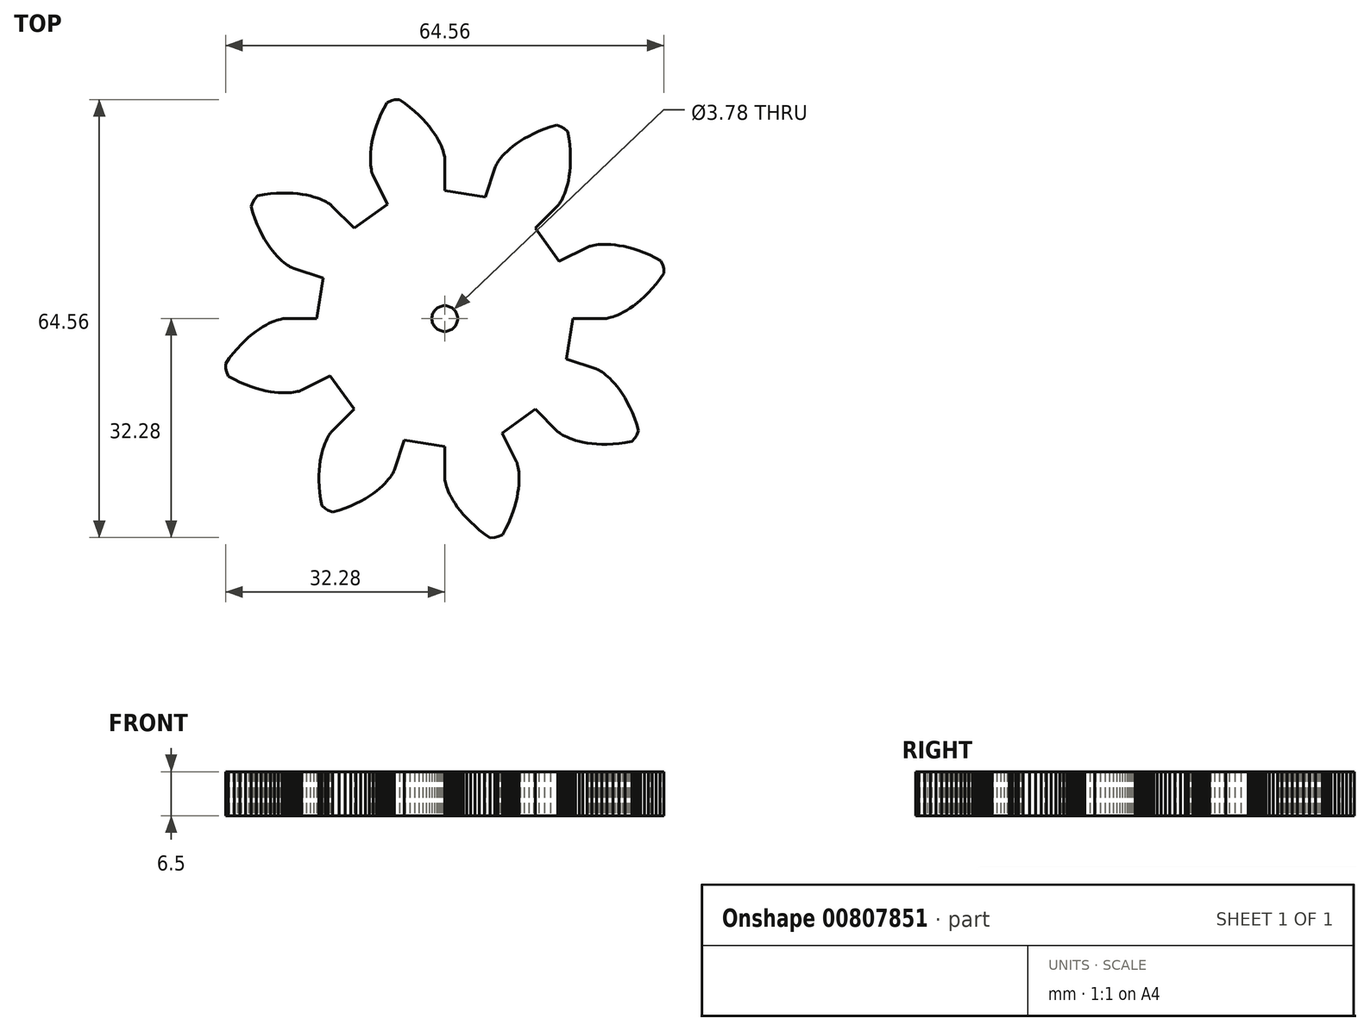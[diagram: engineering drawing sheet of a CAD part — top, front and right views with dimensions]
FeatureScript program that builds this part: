
annotation { "Feature Type Name" : "Feature", "Feature Type Description" : "" }
export const myFeature = defineFeature(function(context is Context, id is Id, definition is map)
    precondition{}
    {
        {
            var Q0;
            Q0=qCreatedBy(makeId("Top.planeOp"),FACE);
            var sketch = newSketch(context, id + "F0", { "sketchPlane" : qUnion([Q0])});
            skLineSegment(sketch, "E0", {"start": v(18.85, 0) * mm, "end": v(23.58, 0) * mm});
            skLineSegment(sketch, "E1", {"start": v(23.58, 0) * mm, "end": v(23.62, 0) * mm});
            skLineSegment(sketch, "E2", {"start": v(23.62, 0) * mm, "end": v(23.7, 0) * mm});
            skLineSegment(sketch, "E3", {"start": v(23.7, 0) * mm, "end": v(23.83, 0.03) * mm});
            skLineSegment(sketch, "E4", {"start": v(23.83, 0.03) * mm, "end": v(24, 0.05) * mm});
            skLineSegment(sketch, "E5", {"start": v(24, 0.05) * mm, "end": v(24.22, 0.1) * mm});
            skLineSegment(sketch, "E6", {"start": v(24.22, 0.1) * mm, "end": v(24.48, 0.17) * mm});
            skLineSegment(sketch, "E7", {"start": v(24.48, 0.17) * mm, "end": v(24.77, 0.26) * mm});
            skLineSegment(sketch, "E8", {"start": v(24.77, 0.26) * mm, "end": v(25.1, 0.38) * mm});
            skLineSegment(sketch, "E9", {"start": v(25.1, 0.38) * mm, "end": v(25.47, 0.53) * mm});
            skLineSegment(sketch, "E10", {"start": v(25.47, 0.53) * mm, "end": v(25.88, 0.72) * mm});
            skLineSegment(sketch, "E11", {"start": v(25.88, 0.72) * mm, "end": v(26.31, 0.94) * mm});
            skLineSegment(sketch, "E12", {"start": v(26.31, 0.94) * mm, "end": v(26.78, 1.2) * mm});
            skLineSegment(sketch, "E13", {"start": v(26.78, 1.2) * mm, "end": v(27.27, 1.52) * mm});
            skLineSegment(sketch, "E14", {"start": v(27.27, 1.52) * mm, "end": v(27.78, 1.87) * mm});
            skLineSegment(sketch, "E15", {"start": v(27.78, 1.87) * mm, "end": v(28.31, 2.28) * mm});
            skLineSegment(sketch, "E16", {"start": v(28.31, 2.28) * mm, "end": v(28.86, 2.73) * mm});
            skLineSegment(sketch, "E17", {"start": v(28.86, 2.73) * mm, "end": v(29.42, 3.25) * mm});
            skLineSegment(sketch, "E18", {"start": v(29.42, 3.25) * mm, "end": v(30, 3.81) * mm});
            skLineSegment(sketch, "E19", {"start": v(30, 3.81) * mm, "end": v(30.57, 4.43) * mm});
            skLineSegment(sketch, "E20", {"start": v(30.57, 4.43) * mm, "end": v(31.14, 5.12) * mm});
            skLineSegment(sketch, "E21", {"start": v(31.14, 5.12) * mm, "end": v(31.72, 5.86) * mm});
            skLineSegment(sketch, "E22", {"start": v(31.72, 5.86) * mm, "end": v(32.28, 6.66) * mm});
            skLineSegment(sketch, "E23", {"start": v(32.28, 6.66) * mm, "end": v(32.24, 7.39) * mm});
            skLineSegment(sketch, "E24", {"start": v(32.24, 7.39) * mm, "end": v(32.13, 7.83) * mm});
            skLineSegment(sketch, "E25", {"start": v(32.13, 7.83) * mm, "end": v(31.85, 8.5) * mm});
            skLineSegment(sketch, "E26", {"start": v(31.85, 8.5) * mm, "end": v(30.98, 8.97) * mm});
            skLineSegment(sketch, "E27", {"start": v(30.98, 8.97) * mm, "end": v(30.14, 9.37) * mm});
            skLineSegment(sketch, "E28", {"start": v(30.14, 9.37) * mm, "end": v(29.31, 9.73) * mm});
            skLineSegment(sketch, "E29", {"start": v(29.31, 9.73) * mm, "end": v(28.52, 10.03) * mm});
            skLineSegment(sketch, "E30", {"start": v(28.52, 10.03) * mm, "end": v(27.76, 10.28) * mm});
            skLineSegment(sketch, "E31", {"start": v(27.76, 10.28) * mm, "end": v(27.03, 10.48) * mm});
            skLineSegment(sketch, "E32", {"start": v(27.03, 10.48) * mm, "end": v(26.33, 10.64) * mm});
            skLineSegment(sketch, "E33", {"start": v(26.33, 10.64) * mm, "end": v(25.68, 10.77) * mm});
            skLineSegment(sketch, "E34", {"start": v(25.68, 10.77) * mm, "end": v(25.06, 10.85) * mm});
            skLineSegment(sketch, "E35", {"start": v(25.06, 10.85) * mm, "end": v(24.48, 10.91) * mm});
            skLineSegment(sketch, "E36", {"start": v(24.48, 10.91) * mm, "end": v(23.95, 10.94) * mm});
            skLineSegment(sketch, "E37", {"start": v(23.95, 10.94) * mm, "end": v(23.46, 10.95) * mm});
            skLineSegment(sketch, "E38", {"start": v(23.46, 10.95) * mm, "end": v(23.02, 10.93) * mm});
            skLineSegment(sketch, "E39", {"start": v(23.02, 10.93) * mm, "end": v(22.62, 10.9) * mm});
            skLineSegment(sketch, "E40", {"start": v(22.62, 10.9) * mm, "end": v(22.26, 10.86) * mm});
            skLineSegment(sketch, "E41", {"start": v(22.26, 10.86) * mm, "end": v(21.96, 10.81) * mm});
            skLineSegment(sketch, "E42", {"start": v(21.96, 10.81) * mm, "end": v(21.7, 10.76) * mm});
            skLineSegment(sketch, "E43", {"start": v(21.7, 10.76) * mm, "end": v(21.49, 10.7) * mm});
            skLineSegment(sketch, "E44", {"start": v(21.49, 10.7) * mm, "end": v(21.32, 10.65) * mm});
            skLineSegment(sketch, "E45", {"start": v(21.32, 10.65) * mm, "end": v(21.2, 10.6) * mm});
            skLineSegment(sketch, "E46", {"start": v(21.2, 10.6) * mm, "end": v(21.12, 10.58) * mm});
            skLineSegment(sketch, "E47", {"start": v(21.12, 10.58) * mm, "end": v(21.08, 10.56) * mm});
            skLineSegment(sketch, "E48", {"start": v(21.08, 10.56) * mm, "end": v(16.85, 8.44) * mm});
            skLineSegment(sketch, "E49", {"start": v(16.85, 8.44) * mm, "end": v(13.33, 13.33) * mm});
            skLineSegment(sketch, "E50", {"start": v(13.33, 13.33) * mm, "end": v(16.67, 16.67) * mm});
            skLineSegment(sketch, "E51", {"start": v(16.67, 16.67) * mm, "end": v(16.7, 16.7) * mm});
            skLineSegment(sketch, "E52", {"start": v(16.7, 16.7) * mm, "end": v(16.75, 16.77) * mm});
            skLineSegment(sketch, "E53", {"start": v(16.75, 16.77) * mm, "end": v(16.83, 16.87) * mm});
            skLineSegment(sketch, "E54", {"start": v(16.83, 16.87) * mm, "end": v(16.93, 17.01) * mm});
            skLineSegment(sketch, "E55", {"start": v(16.93, 17.01) * mm, "end": v(17.05, 17.2) * mm});
            skLineSegment(sketch, "E56", {"start": v(17.05, 17.2) * mm, "end": v(17.19, 17.43) * mm});
            skLineSegment(sketch, "E57", {"start": v(17.19, 17.43) * mm, "end": v(17.33, 17.7) * mm});
            skLineSegment(sketch, "E58", {"start": v(17.33, 17.7) * mm, "end": v(17.48, 18.02) * mm});
            skLineSegment(sketch, "E59", {"start": v(17.48, 18.02) * mm, "end": v(17.64, 18.39) * mm});
            skLineSegment(sketch, "E60", {"start": v(17.64, 18.39) * mm, "end": v(17.8, 18.8) * mm});
            skLineSegment(sketch, "E61", {"start": v(17.8, 18.8) * mm, "end": v(17.94, 19.27) * mm});
            skLineSegment(sketch, "E62", {"start": v(17.94, 19.27) * mm, "end": v(18.08, 19.79) * mm});
            skLineSegment(sketch, "E63", {"start": v(18.08, 19.79) * mm, "end": v(18.2, 20.35) * mm});
            skLineSegment(sketch, "E64", {"start": v(18.2, 20.35) * mm, "end": v(18.32, 20.97) * mm});
            skLineSegment(sketch, "E65", {"start": v(18.32, 20.97) * mm, "end": v(18.4, 21.63) * mm});
            skLineSegment(sketch, "E66", {"start": v(18.4, 21.63) * mm, "end": v(18.47, 22.34) * mm});
            skLineSegment(sketch, "E67", {"start": v(18.47, 22.34) * mm, "end": v(18.5, 23.1) * mm});
            skLineSegment(sketch, "E68", {"start": v(18.5, 23.1) * mm, "end": v(18.51, 23.9) * mm});
            skLineSegment(sketch, "E69", {"start": v(18.51, 23.9) * mm, "end": v(18.48, 24.75) * mm});
            skLineSegment(sketch, "E70", {"start": v(18.48, 24.75) * mm, "end": v(18.4, 25.64) * mm});
            skLineSegment(sketch, "E71", {"start": v(18.4, 25.64) * mm, "end": v(18.29, 26.57) * mm});
            skLineSegment(sketch, "E72", {"start": v(18.29, 26.57) * mm, "end": v(18.12, 27.54) * mm});
            skLineSegment(sketch, "E73", {"start": v(18.12, 27.54) * mm, "end": v(17.57, 28.02) * mm});
            skLineSegment(sketch, "E74", {"start": v(17.57, 28.02) * mm, "end": v(17.18, 28.26) * mm});
            skLineSegment(sketch, "E75", {"start": v(17.18, 28.26) * mm, "end": v(16.5, 28.53) * mm});
            skLineSegment(sketch, "E76", {"start": v(16.5, 28.53) * mm, "end": v(15.57, 28.25) * mm});
            skLineSegment(sketch, "E77", {"start": v(15.57, 28.25) * mm, "end": v(14.68, 27.94) * mm});
            skLineSegment(sketch, "E78", {"start": v(14.68, 27.94) * mm, "end": v(13.85, 27.6) * mm});
            skLineSegment(sketch, "E79", {"start": v(13.85, 27.6) * mm, "end": v(13.08, 27.26) * mm});
            skLineSegment(sketch, "E80", {"start": v(13.08, 27.26) * mm, "end": v(12.36, 26.9) * mm});
            skLineSegment(sketch, "E81", {"start": v(12.36, 26.9) * mm, "end": v(11.7, 26.52) * mm});
            skLineSegment(sketch, "E82", {"start": v(11.7, 26.52) * mm, "end": v(11.1, 26.15) * mm});
            skLineSegment(sketch, "E83", {"start": v(11.1, 26.15) * mm, "end": v(10.54, 25.77) * mm});
            skLineSegment(sketch, "E84", {"start": v(10.54, 25.77) * mm, "end": v(10.04, 25.4) * mm});
            skLineSegment(sketch, "E85", {"start": v(10.04, 25.4) * mm, "end": v(9.6, 25.03) * mm});
            skLineSegment(sketch, "E86", {"start": v(9.6, 25.03) * mm, "end": v(9.2, 24.67) * mm});
            skLineSegment(sketch, "E87", {"start": v(9.2, 24.67) * mm, "end": v(8.85, 24.33) * mm});
            skLineSegment(sketch, "E88", {"start": v(8.85, 24.33) * mm, "end": v(8.54, 24) * mm});
            skLineSegment(sketch, "E89", {"start": v(8.54, 24) * mm, "end": v(8.28, 23.7) * mm});
            skLineSegment(sketch, "E90", {"start": v(8.28, 23.7) * mm, "end": v(8.06, 23.42) * mm});
            skLineSegment(sketch, "E91", {"start": v(8.06, 23.42) * mm, "end": v(7.88, 23.17) * mm});
            skLineSegment(sketch, "E92", {"start": v(7.88, 23.17) * mm, "end": v(7.74, 22.95) * mm});
            skLineSegment(sketch, "E93", {"start": v(7.74, 22.95) * mm, "end": v(7.63, 22.76) * mm});
            skLineSegment(sketch, "E94", {"start": v(7.63, 22.76) * mm, "end": v(7.54, 22.6) * mm});
            skLineSegment(sketch, "E95", {"start": v(7.54, 22.6) * mm, "end": v(7.49, 22.49) * mm});
            skLineSegment(sketch, "E96", {"start": v(7.49, 22.49) * mm, "end": v(7.45, 22.41) * mm});
            skLineSegment(sketch, "E97", {"start": v(7.45, 22.41) * mm, "end": v(7.44, 22.37) * mm});
            skLineSegment(sketch, "E98", {"start": v(7.44, 22.37) * mm, "end": v(5.95, 17.89) * mm});
            skLineSegment(sketch, "E99", {"start": v(5.95, 17.89) * mm, "end": v(0, 18.85) * mm});
            skLineSegment(sketch, "E100", {"start": v(0, 18.85) * mm, "end": v(0, 23.58) * mm});
            skLineSegment(sketch, "E101", {"start": v(0, 23.58) * mm, "end": v(0, 23.62) * mm});
            skLineSegment(sketch, "E102", {"start": v(0, 23.62) * mm, "end": v(0, 23.7) * mm});
            skLineSegment(sketch, "E103", {"start": v(0, 23.7) * mm, "end": v(-0.03, 23.83) * mm});
            skLineSegment(sketch, "E104", {"start": v(-0.03, 23.83) * mm, "end": v(-0.06, 24) * mm});
            skLineSegment(sketch, "E105", {"start": v(-0.06, 24) * mm, "end": v(-0.1, 24.22) * mm});
            skLineSegment(sketch, "E106", {"start": v(-0.1, 24.22) * mm, "end": v(-0.17, 24.48) * mm});
            skLineSegment(sketch, "E107", {"start": v(-0.17, 24.48) * mm, "end": v(-0.26, 24.77) * mm});
            skLineSegment(sketch, "E108", {"start": v(-0.26, 24.77) * mm, "end": v(-0.38, 25.1) * mm});
            skLineSegment(sketch, "E109", {"start": v(-0.38, 25.1) * mm, "end": v(-0.53, 25.47) * mm});
            skLineSegment(sketch, "E110", {"start": v(-0.53, 25.47) * mm, "end": v(-0.72, 25.88) * mm});
            skLineSegment(sketch, "E111", {"start": v(-0.72, 25.88) * mm, "end": v(-0.94, 26.31) * mm});
            skLineSegment(sketch, "E112", {"start": v(-0.94, 26.31) * mm, "end": v(-1.2, 26.78) * mm});
            skLineSegment(sketch, "E113", {"start": v(-1.2, 26.78) * mm, "end": v(-1.52, 27.27) * mm});
            skLineSegment(sketch, "E114", {"start": v(-1.52, 27.27) * mm, "end": v(-1.87, 27.78) * mm});
            skLineSegment(sketch, "E115", {"start": v(-1.87, 27.78) * mm, "end": v(-2.28, 28.31) * mm});
            skLineSegment(sketch, "E116", {"start": v(-2.28, 28.31) * mm, "end": v(-2.73, 28.86) * mm});
            skLineSegment(sketch, "E117", {"start": v(-2.73, 28.86) * mm, "end": v(-3.25, 29.42) * mm});
            skLineSegment(sketch, "E118", {"start": v(-3.25, 29.42) * mm, "end": v(-3.81, 30) * mm});
            skLineSegment(sketch, "E119", {"start": v(-3.81, 30) * mm, "end": v(-4.43, 30.57) * mm});
            skLineSegment(sketch, "E120", {"start": v(-4.43, 30.57) * mm, "end": v(-5.12, 31.14) * mm});
            skLineSegment(sketch, "E121", {"start": v(-5.12, 31.14) * mm, "end": v(-5.86, 31.72) * mm});
            skLineSegment(sketch, "E122", {"start": v(-5.86, 31.72) * mm, "end": v(-6.66, 32.28) * mm});
            skLineSegment(sketch, "E123", {"start": v(-6.66, 32.28) * mm, "end": v(-7.39, 32.24) * mm});
            skLineSegment(sketch, "E124", {"start": v(-7.39, 32.24) * mm, "end": v(-7.83, 32.13) * mm});
            skLineSegment(sketch, "E125", {"start": v(-7.83, 32.13) * mm, "end": v(-8.5, 31.85) * mm});
            skLineSegment(sketch, "E126", {"start": v(-8.5, 31.85) * mm, "end": v(-8.97, 30.98) * mm});
            skLineSegment(sketch, "E127", {"start": v(-8.97, 30.98) * mm, "end": v(-9.37, 30.14) * mm});
            skLineSegment(sketch, "E128", {"start": v(-9.37, 30.14) * mm, "end": v(-9.73, 29.31) * mm});
            skLineSegment(sketch, "E129", {"start": v(-9.73, 29.31) * mm, "end": v(-10.03, 28.52) * mm});
            skLineSegment(sketch, "E130", {"start": v(-10.03, 28.52) * mm, "end": v(-10.28, 27.76) * mm});
            skLineSegment(sketch, "E131", {"start": v(-10.28, 27.76) * mm, "end": v(-10.48, 27.03) * mm});
            skLineSegment(sketch, "E132", {"start": v(-10.48, 27.03) * mm, "end": v(-10.64, 26.33) * mm});
            skLineSegment(sketch, "E133", {"start": v(-10.64, 26.33) * mm, "end": v(-10.77, 25.68) * mm});
            skLineSegment(sketch, "E134", {"start": v(-10.77, 25.68) * mm, "end": v(-10.85, 25.06) * mm});
            skLineSegment(sketch, "E135", {"start": v(-10.85, 25.06) * mm, "end": v(-10.91, 24.48) * mm});
            skLineSegment(sketch, "E136", {"start": v(-10.91, 24.48) * mm, "end": v(-10.94, 23.95) * mm});
            skLineSegment(sketch, "E137", {"start": v(-10.94, 23.95) * mm, "end": v(-10.95, 23.46) * mm});
            skLineSegment(sketch, "E138", {"start": v(-10.95, 23.46) * mm, "end": v(-10.93, 23.02) * mm});
            skLineSegment(sketch, "E139", {"start": v(-10.93, 23.02) * mm, "end": v(-10.9, 22.62) * mm});
            skLineSegment(sketch, "E140", {"start": v(-10.9, 22.62) * mm, "end": v(-10.86, 22.26) * mm});
            skLineSegment(sketch, "E141", {"start": v(-10.86, 22.26) * mm, "end": v(-10.81, 21.96) * mm});
            skLineSegment(sketch, "E142", {"start": v(-10.81, 21.96) * mm, "end": v(-10.76, 21.7) * mm});
            skLineSegment(sketch, "E143", {"start": v(-10.76, 21.7) * mm, "end": v(-10.7, 21.49) * mm});
            skLineSegment(sketch, "E144", {"start": v(-10.7, 21.49) * mm, "end": v(-10.65, 21.32) * mm});
            skLineSegment(sketch, "E145", {"start": v(-10.65, 21.32) * mm, "end": v(-10.6, 21.2) * mm});
            skLineSegment(sketch, "E146", {"start": v(-10.6, 21.2) * mm, "end": v(-10.58, 21.12) * mm});
            skLineSegment(sketch, "E147", {"start": v(-10.58, 21.12) * mm, "end": v(-10.56, 21.08) * mm});
            skLineSegment(sketch, "E148", {"start": v(-10.56, 21.08) * mm, "end": v(-8.44, 16.85) * mm});
            skLineSegment(sketch, "E149", {"start": v(-8.44, 16.85) * mm, "end": v(-13.33, 13.33) * mm});
            skLineSegment(sketch, "E150", {"start": v(-13.33, 13.33) * mm, "end": v(-16.67, 16.67) * mm});
            skLineSegment(sketch, "E151", {"start": v(-16.67, 16.67) * mm, "end": v(-16.7, 16.7) * mm});
            skLineSegment(sketch, "E152", {"start": v(-16.7, 16.7) * mm, "end": v(-16.77, 16.75) * mm});
            skLineSegment(sketch, "E153", {"start": v(-16.77, 16.75) * mm, "end": v(-16.87, 16.83) * mm});
            skLineSegment(sketch, "E154", {"start": v(-16.87, 16.83) * mm, "end": v(-17.01, 16.93) * mm});
            skLineSegment(sketch, "E155", {"start": v(-17.01, 16.93) * mm, "end": v(-17.2, 17.05) * mm});
            skLineSegment(sketch, "E156", {"start": v(-17.2, 17.05) * mm, "end": v(-17.43, 17.19) * mm});
            skLineSegment(sketch, "E157", {"start": v(-17.43, 17.19) * mm, "end": v(-17.7, 17.33) * mm});
            skLineSegment(sketch, "E158", {"start": v(-17.7, 17.33) * mm, "end": v(-18.02, 17.48) * mm});
            skLineSegment(sketch, "E159", {"start": v(-18.02, 17.48) * mm, "end": v(-18.4, 17.64) * mm});
            skLineSegment(sketch, "E160", {"start": v(-18.4, 17.64) * mm, "end": v(-18.8, 17.8) * mm});
            skLineSegment(sketch, "E161", {"start": v(-18.8, 17.8) * mm, "end": v(-19.27, 17.94) * mm});
            skLineSegment(sketch, "E162", {"start": v(-19.27, 17.94) * mm, "end": v(-19.79, 18.08) * mm});
            skLineSegment(sketch, "E163", {"start": v(-19.79, 18.08) * mm, "end": v(-20.35, 18.2) * mm});
            skLineSegment(sketch, "E164", {"start": v(-20.35, 18.2) * mm, "end": v(-20.97, 18.32) * mm});
            skLineSegment(sketch, "E165", {"start": v(-20.97, 18.32) * mm, "end": v(-21.63, 18.4) * mm});
            skLineSegment(sketch, "E166", {"start": v(-21.63, 18.4) * mm, "end": v(-22.34, 18.47) * mm});
            skLineSegment(sketch, "E167", {"start": v(-22.34, 18.47) * mm, "end": v(-23.1, 18.5) * mm});
            skLineSegment(sketch, "E168", {"start": v(-23.1, 18.5) * mm, "end": v(-23.9, 18.51) * mm});
            skLineSegment(sketch, "E169", {"start": v(-23.9, 18.51) * mm, "end": v(-24.75, 18.48) * mm});
            skLineSegment(sketch, "E170", {"start": v(-24.75, 18.48) * mm, "end": v(-25.64, 18.4) * mm});
            skLineSegment(sketch, "E171", {"start": v(-25.64, 18.4) * mm, "end": v(-26.57, 18.29) * mm});
            skLineSegment(sketch, "E172", {"start": v(-26.57, 18.29) * mm, "end": v(-27.54, 18.12) * mm});
            skLineSegment(sketch, "E173", {"start": v(-27.54, 18.12) * mm, "end": v(-28.02, 17.57) * mm});
            skLineSegment(sketch, "E174", {"start": v(-28.02, 17.57) * mm, "end": v(-28.26, 17.18) * mm});
            skLineSegment(sketch, "E175", {"start": v(-28.26, 17.18) * mm, "end": v(-28.53, 16.5) * mm});
            skLineSegment(sketch, "E176", {"start": v(-28.53, 16.5) * mm, "end": v(-28.25, 15.57) * mm});
            skLineSegment(sketch, "E177", {"start": v(-28.25, 15.57) * mm, "end": v(-27.94, 14.68) * mm});
            skLineSegment(sketch, "E178", {"start": v(-27.94, 14.68) * mm, "end": v(-27.6, 13.85) * mm});
            skLineSegment(sketch, "E179", {"start": v(-27.6, 13.85) * mm, "end": v(-27.26, 13.08) * mm});
            skLineSegment(sketch, "E180", {"start": v(-27.26, 13.08) * mm, "end": v(-26.9, 12.36) * mm});
            skLineSegment(sketch, "E181", {"start": v(-26.9, 12.36) * mm, "end": v(-26.52, 11.7) * mm});
            skLineSegment(sketch, "E182", {"start": v(-26.52, 11.7) * mm, "end": v(-26.15, 11.1) * mm});
            skLineSegment(sketch, "E183", {"start": v(-26.15, 11.1) * mm, "end": v(-25.77, 10.54) * mm});
            skLineSegment(sketch, "E184", {"start": v(-25.77, 10.54) * mm, "end": v(-25.4, 10.04) * mm});
            skLineSegment(sketch, "E185", {"start": v(-25.4, 10.04) * mm, "end": v(-25.03, 9.6) * mm});
            skLineSegment(sketch, "E186", {"start": v(-25.03, 9.6) * mm, "end": v(-24.67, 9.2) * mm});
            skLineSegment(sketch, "E187", {"start": v(-24.67, 9.2) * mm, "end": v(-24.33, 8.85) * mm});
            skLineSegment(sketch, "E188", {"start": v(-24.33, 8.85) * mm, "end": v(-24, 8.54) * mm});
            skLineSegment(sketch, "E189", {"start": v(-24, 8.54) * mm, "end": v(-23.7, 8.28) * mm});
            skLineSegment(sketch, "E190", {"start": v(-23.7, 8.28) * mm, "end": v(-23.42, 8.06) * mm});
            skLineSegment(sketch, "E191", {"start": v(-23.42, 8.06) * mm, "end": v(-23.17, 7.88) * mm});
            skLineSegment(sketch, "E192", {"start": v(-23.17, 7.88) * mm, "end": v(-22.95, 7.74) * mm});
            skLineSegment(sketch, "E193", {"start": v(-22.95, 7.74) * mm, "end": v(-22.76, 7.63) * mm});
            skLineSegment(sketch, "E194", {"start": v(-22.76, 7.63) * mm, "end": v(-22.6, 7.54) * mm});
            skLineSegment(sketch, "E195", {"start": v(-22.6, 7.54) * mm, "end": v(-22.49, 7.49) * mm});
            skLineSegment(sketch, "E196", {"start": v(-22.49, 7.49) * mm, "end": v(-22.41, 7.45) * mm});
            skLineSegment(sketch, "E197", {"start": v(-22.41, 7.45) * mm, "end": v(-22.37, 7.44) * mm});
            skLineSegment(sketch, "E198", {"start": v(-22.37, 7.44) * mm, "end": v(-17.89, 5.95) * mm});
            skLineSegment(sketch, "E199", {"start": v(-17.89, 5.95) * mm, "end": v(-18.85, 0) * mm});
            skLineSegment(sketch, "E200", {"start": v(-18.85, 0) * mm, "end": v(-23.58, 0) * mm});
            skLineSegment(sketch, "E201", {"start": v(-23.58, 0) * mm, "end": v(-23.62, 0) * mm});
            skLineSegment(sketch, "E202", {"start": v(-23.62, 0) * mm, "end": v(-23.7, 0) * mm});
            skLineSegment(sketch, "E203", {"start": v(-23.7, 0) * mm, "end": v(-23.83, -0.03) * mm});
            skLineSegment(sketch, "E204", {"start": v(-23.83, -0.03) * mm, "end": v(-24, -0.06) * mm});
            skLineSegment(sketch, "E205", {"start": v(-24, -0.06) * mm, "end": v(-24.22, -0.1) * mm});
            skLineSegment(sketch, "E206", {"start": v(-24.22, -0.1) * mm, "end": v(-24.48, -0.17) * mm});
            skLineSegment(sketch, "E207", {"start": v(-24.48, -0.17) * mm, "end": v(-24.77, -0.26) * mm});
            skLineSegment(sketch, "E208", {"start": v(-24.77, -0.26) * mm, "end": v(-25.1, -0.38) * mm});
            skLineSegment(sketch, "E209", {"start": v(-25.1, -0.38) * mm, "end": v(-25.47, -0.53) * mm});
            skLineSegment(sketch, "E210", {"start": v(-25.47, -0.53) * mm, "end": v(-25.88, -0.72) * mm});
            skLineSegment(sketch, "E211", {"start": v(-25.88, -0.72) * mm, "end": v(-26.31, -0.94) * mm});
            skLineSegment(sketch, "E212", {"start": v(-26.31, -0.94) * mm, "end": v(-26.78, -1.2) * mm});
            skLineSegment(sketch, "E213", {"start": v(-26.78, -1.2) * mm, "end": v(-27.27, -1.52) * mm});
            skLineSegment(sketch, "E214", {"start": v(-27.27, -1.52) * mm, "end": v(-27.78, -1.87) * mm});
            skLineSegment(sketch, "E215", {"start": v(-27.78, -1.87) * mm, "end": v(-28.31, -2.28) * mm});
            skLineSegment(sketch, "E216", {"start": v(-28.31, -2.28) * mm, "end": v(-28.86, -2.73) * mm});
            skLineSegment(sketch, "E217", {"start": v(-28.86, -2.73) * mm, "end": v(-29.42, -3.25) * mm});
            skLineSegment(sketch, "E218", {"start": v(-29.42, -3.25) * mm, "end": v(-30, -3.81) * mm});
            skLineSegment(sketch, "E219", {"start": v(-30, -3.81) * mm, "end": v(-30.57, -4.43) * mm});
            skLineSegment(sketch, "E220", {"start": v(-30.57, -4.43) * mm, "end": v(-31.14, -5.12) * mm});
            skLineSegment(sketch, "E221", {"start": v(-31.14, -5.12) * mm, "end": v(-31.72, -5.86) * mm});
            skLineSegment(sketch, "E222", {"start": v(-31.72, -5.86) * mm, "end": v(-32.28, -6.66) * mm});
            skLineSegment(sketch, "E223", {"start": v(-32.28, -6.66) * mm, "end": v(-32.24, -7.39) * mm});
            skLineSegment(sketch, "E224", {"start": v(-32.24, -7.39) * mm, "end": v(-32.13, -7.83) * mm});
            skLineSegment(sketch, "E225", {"start": v(-32.13, -7.83) * mm, "end": v(-31.85, -8.5) * mm});
            skLineSegment(sketch, "E226", {"start": v(-31.85, -8.5) * mm, "end": v(-30.98, -8.97) * mm});
            skLineSegment(sketch, "E227", {"start": v(-30.98, -8.97) * mm, "end": v(-30.14, -9.37) * mm});
            skLineSegment(sketch, "E228", {"start": v(-30.14, -9.37) * mm, "end": v(-29.32, -9.73) * mm});
            skLineSegment(sketch, "E229", {"start": v(-29.32, -9.73) * mm, "end": v(-28.52, -10.03) * mm});
            skLineSegment(sketch, "E230", {"start": v(-28.52, -10.03) * mm, "end": v(-27.76, -10.28) * mm});
            skLineSegment(sketch, "E231", {"start": v(-27.76, -10.28) * mm, "end": v(-27.03, -10.48) * mm});
            skLineSegment(sketch, "E232", {"start": v(-27.03, -10.48) * mm, "end": v(-26.33, -10.64) * mm});
            skLineSegment(sketch, "E233", {"start": v(-26.33, -10.64) * mm, "end": v(-25.68, -10.77) * mm});
            skLineSegment(sketch, "E234", {"start": v(-25.68, -10.77) * mm, "end": v(-25.06, -10.85) * mm});
            skLineSegment(sketch, "E235", {"start": v(-25.06, -10.85) * mm, "end": v(-24.48, -10.91) * mm});
            skLineSegment(sketch, "E236", {"start": v(-24.48, -10.91) * mm, "end": v(-23.95, -10.94) * mm});
            skLineSegment(sketch, "E237", {"start": v(-23.95, -10.94) * mm, "end": v(-23.46, -10.95) * mm});
            skLineSegment(sketch, "E238", {"start": v(-23.46, -10.95) * mm, "end": v(-23.02, -10.93) * mm});
            skLineSegment(sketch, "E239", {"start": v(-23.02, -10.93) * mm, "end": v(-22.62, -10.9) * mm});
            skLineSegment(sketch, "E240", {"start": v(-22.62, -10.9) * mm, "end": v(-22.27, -10.86) * mm});
            skLineSegment(sketch, "E241", {"start": v(-22.27, -10.86) * mm, "end": v(-21.96, -10.81) * mm});
            skLineSegment(sketch, "E242", {"start": v(-21.96, -10.81) * mm, "end": v(-21.7, -10.76) * mm});
            skLineSegment(sketch, "E243", {"start": v(-21.7, -10.76) * mm, "end": v(-21.49, -10.7) * mm});
            skLineSegment(sketch, "E244", {"start": v(-21.49, -10.7) * mm, "end": v(-21.32, -10.65) * mm});
            skLineSegment(sketch, "E245", {"start": v(-21.32, -10.65) * mm, "end": v(-21.2, -10.6) * mm});
            skLineSegment(sketch, "E246", {"start": v(-21.2, -10.6) * mm, "end": v(-21.12, -10.58) * mm});
            skLineSegment(sketch, "E247", {"start": v(-21.12, -10.58) * mm, "end": v(-21.08, -10.56) * mm});
            skLineSegment(sketch, "E248", {"start": v(-21.08, -10.56) * mm, "end": v(-16.85, -8.44) * mm});
            skLineSegment(sketch, "E249", {"start": v(-16.85, -8.44) * mm, "end": v(-13.33, -13.33) * mm});
            skLineSegment(sketch, "E250", {"start": v(-13.33, -13.33) * mm, "end": v(-16.67, -16.67) * mm});
            skLineSegment(sketch, "E251", {"start": v(-16.67, -16.67) * mm, "end": v(-16.7, -16.7) * mm});
            skLineSegment(sketch, "E252", {"start": v(-16.7, -16.7) * mm, "end": v(-16.75, -16.77) * mm});
            skLineSegment(sketch, "E253", {"start": v(-16.75, -16.77) * mm, "end": v(-16.83, -16.87) * mm});
            skLineSegment(sketch, "E254", {"start": v(-16.83, -16.87) * mm, "end": v(-16.93, -17.01) * mm});
            skLineSegment(sketch, "E255", {"start": v(-16.93, -17.01) * mm, "end": v(-17.05, -17.2) * mm});
            skLineSegment(sketch, "E256", {"start": v(-17.05, -17.2) * mm, "end": v(-17.19, -17.43) * mm});
            skLineSegment(sketch, "E257", {"start": v(-17.19, -17.43) * mm, "end": v(-17.33, -17.7) * mm});
            skLineSegment(sketch, "E258", {"start": v(-17.33, -17.7) * mm, "end": v(-17.48, -18.02) * mm});
            skLineSegment(sketch, "E259", {"start": v(-17.48, -18.02) * mm, "end": v(-17.64, -18.4) * mm});
            skLineSegment(sketch, "E260", {"start": v(-17.64, -18.4) * mm, "end": v(-17.8, -18.8) * mm});
            skLineSegment(sketch, "E261", {"start": v(-17.8, -18.8) * mm, "end": v(-17.94, -19.27) * mm});
            skLineSegment(sketch, "E262", {"start": v(-17.94, -19.27) * mm, "end": v(-18.08, -19.79) * mm});
            skLineSegment(sketch, "E263", {"start": v(-18.08, -19.79) * mm, "end": v(-18.2, -20.35) * mm});
            skLineSegment(sketch, "E264", {"start": v(-18.2, -20.35) * mm, "end": v(-18.32, -20.97) * mm});
            skLineSegment(sketch, "E265", {"start": v(-18.32, -20.97) * mm, "end": v(-18.4, -21.63) * mm});
            skLineSegment(sketch, "E266", {"start": v(-18.4, -21.63) * mm, "end": v(-18.47, -22.34) * mm});
            skLineSegment(sketch, "E267", {"start": v(-18.47, -22.34) * mm, "end": v(-18.5, -23.1) * mm});
            skLineSegment(sketch, "E268", {"start": v(-18.5, -23.1) * mm, "end": v(-18.51, -23.9) * mm});
            skLineSegment(sketch, "E269", {"start": v(-18.51, -23.9) * mm, "end": v(-18.48, -24.75) * mm});
            skLineSegment(sketch, "E270", {"start": v(-18.48, -24.75) * mm, "end": v(-18.4, -25.64) * mm});
            skLineSegment(sketch, "E271", {"start": v(-18.4, -25.64) * mm, "end": v(-18.29, -26.57) * mm});
            skLineSegment(sketch, "E272", {"start": v(-18.29, -26.57) * mm, "end": v(-18.12, -27.54) * mm});
            skLineSegment(sketch, "E273", {"start": v(-18.12, -27.54) * mm, "end": v(-17.57, -28.02) * mm});
            skLineSegment(sketch, "E274", {"start": v(-17.57, -28.02) * mm, "end": v(-17.18, -28.26) * mm});
            skLineSegment(sketch, "E275", {"start": v(-17.18, -28.26) * mm, "end": v(-16.5, -28.53) * mm});
            skLineSegment(sketch, "E276", {"start": v(-16.5, -28.53) * mm, "end": v(-15.57, -28.25) * mm});
            skLineSegment(sketch, "E277", {"start": v(-15.57, -28.25) * mm, "end": v(-14.68, -27.94) * mm});
            skLineSegment(sketch, "E278", {"start": v(-14.68, -27.94) * mm, "end": v(-13.85, -27.6) * mm});
            skLineSegment(sketch, "E279", {"start": v(-13.85, -27.6) * mm, "end": v(-13.08, -27.26) * mm});
            skLineSegment(sketch, "E280", {"start": v(-13.08, -27.26) * mm, "end": v(-12.36, -26.9) * mm});
            skLineSegment(sketch, "E281", {"start": v(-12.36, -26.9) * mm, "end": v(-11.7, -26.52) * mm});
            skLineSegment(sketch, "E282", {"start": v(-11.7, -26.52) * mm, "end": v(-11.1, -26.15) * mm});
            skLineSegment(sketch, "E283", {"start": v(-11.1, -26.15) * mm, "end": v(-10.54, -25.77) * mm});
            skLineSegment(sketch, "E284", {"start": v(-10.54, -25.77) * mm, "end": v(-10.04, -25.4) * mm});
            skLineSegment(sketch, "E285", {"start": v(-10.04, -25.4) * mm, "end": v(-9.6, -25.03) * mm});
            skLineSegment(sketch, "E286", {"start": v(-9.6, -25.03) * mm, "end": v(-9.2, -24.67) * mm});
            skLineSegment(sketch, "E287", {"start": v(-9.2, -24.67) * mm, "end": v(-8.85, -24.33) * mm});
            skLineSegment(sketch, "E288", {"start": v(-8.85, -24.33) * mm, "end": v(-8.54, -24) * mm});
            skLineSegment(sketch, "E289", {"start": v(-8.54, -24) * mm, "end": v(-8.28, -23.7) * mm});
            skLineSegment(sketch, "E290", {"start": v(-8.28, -23.7) * mm, "end": v(-8.06, -23.42) * mm});
            skLineSegment(sketch, "E291", {"start": v(-8.06, -23.42) * mm, "end": v(-7.88, -23.17) * mm});
            skLineSegment(sketch, "E292", {"start": v(-7.88, -23.17) * mm, "end": v(-7.74, -22.95) * mm});
            skLineSegment(sketch, "E293", {"start": v(-7.74, -22.95) * mm, "end": v(-7.63, -22.76) * mm});
            skLineSegment(sketch, "E294", {"start": v(-7.63, -22.76) * mm, "end": v(-7.54, -22.6) * mm});
            skLineSegment(sketch, "E295", {"start": v(-7.54, -22.6) * mm, "end": v(-7.49, -22.49) * mm});
            skLineSegment(sketch, "E296", {"start": v(-7.49, -22.49) * mm, "end": v(-7.45, -22.41) * mm});
            skLineSegment(sketch, "E297", {"start": v(-7.45, -22.41) * mm, "end": v(-7.44, -22.37) * mm});
            skLineSegment(sketch, "E298", {"start": v(-7.44, -22.37) * mm, "end": v(-5.95, -17.89) * mm});
            skLineSegment(sketch, "E299", {"start": v(-5.95, -17.89) * mm, "end": v(0, -18.85) * mm});
            skLineSegment(sketch, "E300", {"start": v(0, -18.85) * mm, "end": v(0, -23.58) * mm});
            skLineSegment(sketch, "E301", {"start": v(0, -23.58) * mm, "end": v(0, -23.62) * mm});
            skLineSegment(sketch, "E302", {"start": v(0, -23.62) * mm, "end": v(0, -23.7) * mm});
            skLineSegment(sketch, "E303", {"start": v(0, -23.7) * mm, "end": v(0.03, -23.83) * mm});
            skLineSegment(sketch, "E304", {"start": v(0.03, -23.83) * mm, "end": v(0.05, -24) * mm});
            skLineSegment(sketch, "E305", {"start": v(0.05, -24) * mm, "end": v(0.1, -24.22) * mm});
            skLineSegment(sketch, "E306", {"start": v(0.1, -24.22) * mm, "end": v(0.17, -24.48) * mm});
            skLineSegment(sketch, "E307", {"start": v(0.17, -24.48) * mm, "end": v(0.26, -24.77) * mm});
            skLineSegment(sketch, "E308", {"start": v(0.26, -24.77) * mm, "end": v(0.38, -25.1) * mm});
            skLineSegment(sketch, "E309", {"start": v(0.38, -25.1) * mm, "end": v(0.53, -25.47) * mm});
            skLineSegment(sketch, "E310", {"start": v(0.53, -25.47) * mm, "end": v(0.72, -25.88) * mm});
            skLineSegment(sketch, "E311", {"start": v(0.72, -25.88) * mm, "end": v(0.94, -26.31) * mm});
            skLineSegment(sketch, "E312", {"start": v(0.94, -26.31) * mm, "end": v(1.2, -26.78) * mm});
            skLineSegment(sketch, "E313", {"start": v(1.2, -26.78) * mm, "end": v(1.52, -27.27) * mm});
            skLineSegment(sketch, "E314", {"start": v(1.52, -27.27) * mm, "end": v(1.87, -27.78) * mm});
            skLineSegment(sketch, "E315", {"start": v(1.87, -27.78) * mm, "end": v(2.28, -28.31) * mm});
            skLineSegment(sketch, "E316", {"start": v(2.28, -28.31) * mm, "end": v(2.73, -28.86) * mm});
            skLineSegment(sketch, "E317", {"start": v(2.73, -28.86) * mm, "end": v(3.25, -29.42) * mm});
            skLineSegment(sketch, "E318", {"start": v(3.25, -29.42) * mm, "end": v(3.81, -30) * mm});
            skLineSegment(sketch, "E319", {"start": v(3.81, -30) * mm, "end": v(4.43, -30.57) * mm});
            skLineSegment(sketch, "E320", {"start": v(4.43, -30.57) * mm, "end": v(5.12, -31.14) * mm});
            skLineSegment(sketch, "E321", {"start": v(5.12, -31.14) * mm, "end": v(5.86, -31.72) * mm});
            skLineSegment(sketch, "E322", {"start": v(5.86, -31.72) * mm, "end": v(6.66, -32.28) * mm});
            skLineSegment(sketch, "E323", {"start": v(6.66, -32.28) * mm, "end": v(7.39, -32.24) * mm});
            skLineSegment(sketch, "E324", {"start": v(7.39, -32.24) * mm, "end": v(7.83, -32.13) * mm});
            skLineSegment(sketch, "E325", {"start": v(7.83, -32.13) * mm, "end": v(8.5, -31.85) * mm});
            skLineSegment(sketch, "E326", {"start": v(8.5, -31.85) * mm, "end": v(8.97, -30.98) * mm});
            skLineSegment(sketch, "E327", {"start": v(8.97, -30.98) * mm, "end": v(9.37, -30.14) * mm});
            skLineSegment(sketch, "E328", {"start": v(9.37, -30.14) * mm, "end": v(9.73, -29.32) * mm});
            skLineSegment(sketch, "E329", {"start": v(9.73, -29.32) * mm, "end": v(10.03, -28.52) * mm});
            skLineSegment(sketch, "E330", {"start": v(10.03, -28.52) * mm, "end": v(10.28, -27.76) * mm});
            skLineSegment(sketch, "E331", {"start": v(10.28, -27.76) * mm, "end": v(10.48, -27.03) * mm});
            skLineSegment(sketch, "E332", {"start": v(10.48, -27.03) * mm, "end": v(10.64, -26.33) * mm});
            skLineSegment(sketch, "E333", {"start": v(10.64, -26.33) * mm, "end": v(10.77, -25.68) * mm});
            skLineSegment(sketch, "E334", {"start": v(10.77, -25.68) * mm, "end": v(10.85, -25.06) * mm});
            skLineSegment(sketch, "E335", {"start": v(10.85, -25.06) * mm, "end": v(10.91, -24.48) * mm});
            skLineSegment(sketch, "E336", {"start": v(10.91, -24.48) * mm, "end": v(10.94, -23.95) * mm});
            skLineSegment(sketch, "E337", {"start": v(10.94, -23.95) * mm, "end": v(10.95, -23.46) * mm});
            skLineSegment(sketch, "E338", {"start": v(10.95, -23.46) * mm, "end": v(10.93, -23.02) * mm});
            skLineSegment(sketch, "E339", {"start": v(10.93, -23.02) * mm, "end": v(10.9, -22.62) * mm});
            skLineSegment(sketch, "E340", {"start": v(10.9, -22.62) * mm, "end": v(10.86, -22.27) * mm});
            skLineSegment(sketch, "E341", {"start": v(10.86, -22.27) * mm, "end": v(10.81, -21.96) * mm});
            skLineSegment(sketch, "E342", {"start": v(10.81, -21.96) * mm, "end": v(10.76, -21.7) * mm});
            skLineSegment(sketch, "E343", {"start": v(10.76, -21.7) * mm, "end": v(10.7, -21.49) * mm});
            skLineSegment(sketch, "E344", {"start": v(10.7, -21.49) * mm, "end": v(10.65, -21.32) * mm});
            skLineSegment(sketch, "E345", {"start": v(10.65, -21.32) * mm, "end": v(10.6, -21.2) * mm});
            skLineSegment(sketch, "E346", {"start": v(10.6, -21.2) * mm, "end": v(10.58, -21.12) * mm});
            skLineSegment(sketch, "E347", {"start": v(10.58, -21.12) * mm, "end": v(10.56, -21.08) * mm});
            skLineSegment(sketch, "E348", {"start": v(10.56, -21.08) * mm, "end": v(8.44, -16.85) * mm});
            skLineSegment(sketch, "E349", {"start": v(8.44, -16.85) * mm, "end": v(13.33, -13.33) * mm});
            skLineSegment(sketch, "E350", {"start": v(13.33, -13.33) * mm, "end": v(16.67, -16.67) * mm});
            skLineSegment(sketch, "E351", {"start": v(16.67, -16.67) * mm, "end": v(16.7, -16.7) * mm});
            skLineSegment(sketch, "E352", {"start": v(16.7, -16.7) * mm, "end": v(16.77, -16.75) * mm});
            skLineSegment(sketch, "E353", {"start": v(16.77, -16.75) * mm, "end": v(16.87, -16.83) * mm});
            skLineSegment(sketch, "E354", {"start": v(16.87, -16.83) * mm, "end": v(17.01, -16.93) * mm});
            skLineSegment(sketch, "E355", {"start": v(17.01, -16.93) * mm, "end": v(17.2, -17.05) * mm});
            skLineSegment(sketch, "E356", {"start": v(17.2, -17.05) * mm, "end": v(17.43, -17.19) * mm});
            skLineSegment(sketch, "E357", {"start": v(17.43, -17.19) * mm, "end": v(17.7, -17.33) * mm});
            skLineSegment(sketch, "E358", {"start": v(17.7, -17.33) * mm, "end": v(18.02, -17.48) * mm});
            skLineSegment(sketch, "E359", {"start": v(18.02, -17.48) * mm, "end": v(18.39, -17.64) * mm});
            skLineSegment(sketch, "E360", {"start": v(18.39, -17.64) * mm, "end": v(18.8, -17.8) * mm});
            skLineSegment(sketch, "E361", {"start": v(18.8, -17.8) * mm, "end": v(19.27, -17.94) * mm});
            skLineSegment(sketch, "E362", {"start": v(19.27, -17.94) * mm, "end": v(19.79, -18.08) * mm});
            skLineSegment(sketch, "E363", {"start": v(19.79, -18.08) * mm, "end": v(20.35, -18.2) * mm});
            skLineSegment(sketch, "E364", {"start": v(20.35, -18.2) * mm, "end": v(20.97, -18.32) * mm});
            skLineSegment(sketch, "E365", {"start": v(20.97, -18.32) * mm, "end": v(21.63, -18.4) * mm});
            skLineSegment(sketch, "E366", {"start": v(21.63, -18.4) * mm, "end": v(22.34, -18.47) * mm});
            skLineSegment(sketch, "E367", {"start": v(22.34, -18.47) * mm, "end": v(23.1, -18.5) * mm});
            skLineSegment(sketch, "E368", {"start": v(23.1, -18.5) * mm, "end": v(23.9, -18.51) * mm});
            skLineSegment(sketch, "E369", {"start": v(23.9, -18.51) * mm, "end": v(24.75, -18.48) * mm});
            skLineSegment(sketch, "E370", {"start": v(24.75, -18.48) * mm, "end": v(25.64, -18.4) * mm});
            skLineSegment(sketch, "E371", {"start": v(25.64, -18.4) * mm, "end": v(26.57, -18.29) * mm});
            skLineSegment(sketch, "E372", {"start": v(26.57, -18.29) * mm, "end": v(27.54, -18.12) * mm});
            skLineSegment(sketch, "E373", {"start": v(27.54, -18.12) * mm, "end": v(28.02, -17.57) * mm});
            skLineSegment(sketch, "E374", {"start": v(28.02, -17.57) * mm, "end": v(28.26, -17.18) * mm});
            skLineSegment(sketch, "E375", {"start": v(28.26, -17.18) * mm, "end": v(28.53, -16.5) * mm});
            skLineSegment(sketch, "E376", {"start": v(28.53, -16.5) * mm, "end": v(28.25, -15.57) * mm});
            skLineSegment(sketch, "E377", {"start": v(28.25, -15.57) * mm, "end": v(27.94, -14.68) * mm});
            skLineSegment(sketch, "E378", {"start": v(27.94, -14.68) * mm, "end": v(27.6, -13.85) * mm});
            skLineSegment(sketch, "E379", {"start": v(27.6, -13.85) * mm, "end": v(27.26, -13.08) * mm});
            skLineSegment(sketch, "E380", {"start": v(27.26, -13.08) * mm, "end": v(26.9, -12.36) * mm});
            skLineSegment(sketch, "E381", {"start": v(26.9, -12.36) * mm, "end": v(26.52, -11.7) * mm});
            skLineSegment(sketch, "E382", {"start": v(26.52, -11.7) * mm, "end": v(26.15, -11.1) * mm});
            skLineSegment(sketch, "E383", {"start": v(26.15, -11.1) * mm, "end": v(25.77, -10.54) * mm});
            skLineSegment(sketch, "E384", {"start": v(25.77, -10.54) * mm, "end": v(25.4, -10.04) * mm});
            skLineSegment(sketch, "E385", {"start": v(25.4, -10.04) * mm, "end": v(25.03, -9.6) * mm});
            skLineSegment(sketch, "E386", {"start": v(25.03, -9.6) * mm, "end": v(24.67, -9.2) * mm});
            skLineSegment(sketch, "E387", {"start": v(24.67, -9.2) * mm, "end": v(24.33, -8.85) * mm});
            skLineSegment(sketch, "E388", {"start": v(24.33, -8.85) * mm, "end": v(24, -8.54) * mm});
            skLineSegment(sketch, "E389", {"start": v(24, -8.54) * mm, "end": v(23.7, -8.28) * mm});
            skLineSegment(sketch, "E390", {"start": v(23.7, -8.28) * mm, "end": v(23.42, -8.06) * mm});
            skLineSegment(sketch, "E391", {"start": v(23.42, -8.06) * mm, "end": v(23.17, -7.88) * mm});
            skLineSegment(sketch, "E392", {"start": v(23.17, -7.88) * mm, "end": v(22.95, -7.74) * mm});
            skLineSegment(sketch, "E393", {"start": v(22.95, -7.74) * mm, "end": v(22.76, -7.63) * mm});
            skLineSegment(sketch, "E394", {"start": v(22.76, -7.63) * mm, "end": v(22.6, -7.54) * mm});
            skLineSegment(sketch, "E395", {"start": v(22.6, -7.54) * mm, "end": v(22.49, -7.49) * mm});
            skLineSegment(sketch, "E396", {"start": v(22.49, -7.49) * mm, "end": v(22.41, -7.45) * mm});
            skLineSegment(sketch, "E397", {"start": v(22.41, -7.45) * mm, "end": v(22.37, -7.44) * mm});
            skLineSegment(sketch, "E398", {"start": v(22.37, -7.44) * mm, "end": v(17.89, -5.95) * mm});
            skLineSegment(sketch, "E399", {"start": v(17.89, -5.95) * mm, "end": v(18.85, 0) * mm});
            skLineSegment(sketch, "E400", {"start": v(2.65, 0) * mm, "end": v(-2.65, 0) * mm});
            skLineSegment(sketch, "E401", {"start": v(0, -2.65) * mm, "end": v(0, 2.65) * mm});
            skCircle(sketch, "E402", {"center": v(0, 0) * mm, "radius": 1.89 * mm});
            skSolve(sketch);
        }
        {
            var Q0;
            Q0=makeQuery(id+"F0.imprint","IMPRINT",FACE,{"disambiguationData":[TD([[makeQuery(id+"F0.imprint","IMPRINT",EDGE,{"derivedFrom":sQuery(id+"F0.wireOp",EDGE,"E0")}),1.0]])]});
            extrude(context, id + "F1", {"entities" : qUnion([Q0]), "depth" : 6.5 * mm, "offsetDistance" : 25 * mm});
        }
    });
